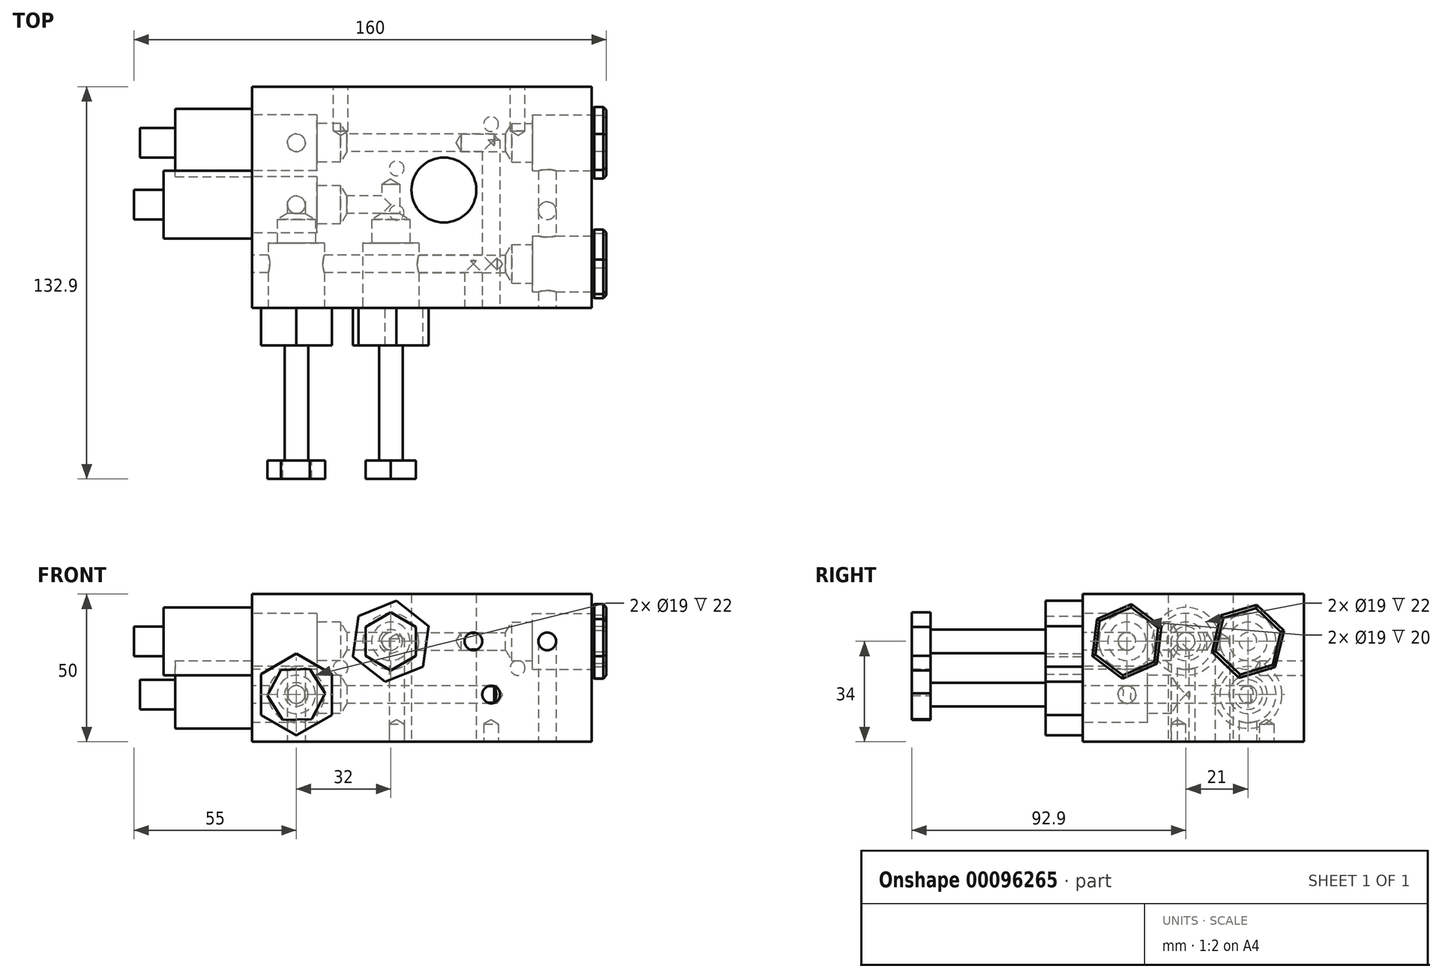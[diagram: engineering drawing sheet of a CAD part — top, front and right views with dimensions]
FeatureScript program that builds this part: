
annotation { "Feature Type Name" : "Feature", "Feature Type Description" : "" }
export const myFeature = defineFeature(function(context is Context, id is Id, definition is map)
    precondition{}
    {
        {
            var Q0;
            Q0=qCreatedBy(makeId("Top.planeOp"),FACE);
            var sketch = newSketch(context, id + "F0", { "sketchPlane" : qUnion([Q0])});
            skLineSegment(sketch, "E0.rect.bottom", {"start": v(50, 35) * mm, "end": v(-65, 35) * mm});
            skLineSegment(sketch, "E0.rect.top", {"start": v(50, -40) * mm, "end": v(-65, -40) * mm});
            skLineSegment(sketch, "E0.rect.left", {"start": v(50, 35) * mm, "end": v(50, -40) * mm});
            skLineSegment(sketch, "E0.rect.right", {"start": v(-65, 35) * mm, "end": v(-65, -40) * mm});
            skPoint(sketch, "E0.rect.middle", {"position": v(0, 0) * mm});
            skSolve(sketch);
        }
        {
            var Q0;
            Q0=makeQuery(id+"F0.imprint","IMPRINT",FACE,{"disambiguationData":[TD([[makeQuery(id+"F0.imprint","IMPRINT",EDGE,{"derivedFrom":sQuery(id+"F0.wireOp",EDGE,"E0.rect.bottom")}),1.0]])]});
            var Q1;
            Q1=makeQuery(id+"F0.imprint","IMPRINT",FACE,{"disambiguationData":[TD([[makeQuery(id+"F0.imprint","IMPRINT",EDGE,{"derivedFrom":sQuery(id+"F0.wireOp",EDGE,"7588558b-6d4b-4371-8287-17bf13519ebf.1.0.0")}),1.0]])]});
            var Q2;
            Q2=makeQuery(id+"F0.imprint","IMPRINT",FACE,{"disambiguationData":[TD([[makeQuery(id+"F0.imprint","IMPRINT",EDGE,{"derivedFrom":sQuery(id+"F0.wireOp",EDGE,"7588558b-6d4b-4371-8287-17bf13519ebf.1.1.0")}),1.0]])]});
            var Q3;
            Q3=makeQuery(id+"F0.imprint","IMPRINT",FACE,{"disambiguationData":[TD([[makeQuery(id+"F0.imprint","IMPRINT",EDGE,{"derivedFrom":sQuery(id+"F0.wireOp",EDGE,"f2f94a69-6f03-48d5-8e05-4ef8c2e551b9")}),1.0]])]});
            var Q4;
            Q4=makeQuery(id+"F0.imprint","IMPRINT",FACE,{"disambiguationData":[TD([[makeQuery(id+"F0.imprint","IMPRINT",EDGE,{"derivedFrom":sQuery(id+"F0.wireOp",EDGE,"7588558b-6d4b-4371-8287-17bf13519ebf.0.1.0")}),1.0]])]});
            extrude(context, id + "F1", {"entities" : qUnion([Q0, Q1, Q2, Q3, Q4]), "depth" : 50 * mm});
        }
        {
            var Q0;
            Q0=makeQuery(id+"F1.opExtrude","CAP_FACE",FACE,{"disambiguationData":[OSD([sQuery(id+"F0.wireOp",EDGE,"E0.rect.bottom"),sQuery(id+"F0.wireOp",EDGE,"E0.rect.top"),sQuery(id+"F0.wireOp",EDGE,"E0.rect.left"),sQuery(id+"F0.wireOp",EDGE,"E0.rect.right"),sQuery(id+"F0.wireOp",EDGE,"fc206ab4-4ad2-4e77-9b30-4fb9f0a5357b")])],"isStart":true});
            var sketch = newSketch(context, id + "F2", { "sketchPlane" : qUnion([Q0])});
            skCircle(sketch, "E1", {"center": v(-16, 7.68) * mm, "radius": 2.75 * mm});
            skCircle(sketch, "E2", {"center": v(16, -22.32) * mm, "radius": 2.75 * mm});
            skCircle(sketch, "E3", {"center": v(-16, -7.32) * mm, "radius": 3 * mm});
            skPoint(sketch, "E4", {"position": v(-50, 5) * mm});
            skPoint(sketch, "E5", {"position": v(35, 7) * mm});
            skPoint(sketch, "E6", {"position": v(-50, -16) * mm});
            skLineSegment(sketch, "E7", {"start": v(-16, -7.32) * mm, "end": v(44.16, -7.32) * mm, "construction": true});
            skLineSegment(sketch, "E8", {"start": v(-16, -16.9) * mm, "end": v(-16, 32.16) * mm, "construction": true});
            skPoint(sketch, "E9.0", {"position": v(0, 0) * mm});
            skLineSegment(sketch, "E10", {"start": v(-80.64, 0) * mm, "end": v(41.16, 0) * mm, "construction": true});
            skSolve(sketch);
        }
        {
            var Q0;
            Q0=sQuery(id+"F2.wireOp",VERTEX,"E3.center");
            var Q1;
            Q1=makeQuery(id+"F1.opExtrude","SWEPT_BODY",BODY,{"disambiguationData":[OSD([sQuery(id+"F0.wireOp",EDGE,"E0.rect.bottom"),sQuery(id+"F0.wireOp",EDGE,"E0.rect.top"),sQuery(id+"F0.wireOp",EDGE,"E0.rect.left"),sQuery(id+"F0.wireOp",EDGE,"E0.rect.right"),sQuery(id+"F0.wireOp",EDGE,"fc206ab4-4ad2-4e77-9b30-4fb9f0a5357b")])]});
            hole(context, id + "F3", {"style" : HoleStyle.SIMPLE, "holeDiameter" : 5 * mm, "endStyle" : HoleEndStyle.BLIND, "holeDepth" : 35 * mm, "locations" : qUnion([Q0]), "scope" : qUnion([Q1])});
        }
        {
            var Q0;
            Q0=makeQuery(id+"F1.opExtrude","SWEPT_FACE",FACE,{"disambiguationData":[OSD([sQuery(id+"F0.wireOp",EDGE,"E0.rect.bottom")])]});
            var sketch = newSketch(context, id + "F4", { "sketchPlane" : qUnion([Q0])});
            skLineSegment(sketch, "E11", {"start": v(65, 16) * mm, "end": v(-50, 16) * mm, "construction": true});
            skPoint(sketch, "E12", {"position": v(-30, 16) * mm});
            skPoint(sketch, "E13", {"position": v(50, 16) * mm});
            skSolve(sketch);
        }
        {
            var Q0;
            Q0=makeQuery(id+"F1.opExtrude","SWEPT_FACE",FACE,{"disambiguationData":[OSD([sQuery(id+"F0.wireOp",EDGE,"E0.rect.left")])]});
            var sketch = newSketch(context, id + "F5", { "sketchPlane" : qUnion([Q0])});
            skLineSegment(sketch, "E14", {"start": v(-25, 34) * mm, "end": v(16, 34) * mm, "construction": true});
            skPoint(sketch, "E15", {"position": v(16, 34) * mm});
            skPoint(sketch, "E16", {"position": v(-25, 34) * mm});
            skPoint(sketch, "E17.orphan", {"position": v(35, 34) * mm});
            skCircle(sketch, "E18.cCircle", {"center": v(-25, 34) * mm, "radius": 11 * mm, "construction": true});
            skLineSegment(sketch, "E18.0", {"start": v(-35.19, 41.58) * mm, "end": v(-23.53, 46.62) * mm});
            skLineSegment(sketch, "E18.1", {"start": v(-23.53, 46.62) * mm, "end": v(-13.34, 39.03) * mm});
            skLineSegment(sketch, "E18.2", {"start": v(-13.34, 39.03) * mm, "end": v(-14.81, 26.42) * mm});
            skLineSegment(sketch, "E18.3", {"start": v(-14.81, 26.42) * mm, "end": v(-26.47, 21.38) * mm});
            skLineSegment(sketch, "E18.4", {"start": v(-26.47, 21.38) * mm, "end": v(-36.66, 28.97) * mm});
            skLineSegment(sketch, "E18.5", {"start": v(-36.66, 28.97) * mm, "end": v(-35.19, 41.58) * mm});
            skPoint(sketch, "E18.0.midPoint", {"position": v(-29.36, 44.1) * mm});
            skCircle(sketch, "E19.cCircle", {"center": v(16, 34) * mm, "radius": 11 * mm, "construction": true});
            skLineSegment(sketch, "E19.0", {"start": v(6.8, 42.75) * mm, "end": v(18.98, 46.35) * mm});
            skLineSegment(sketch, "E19.1", {"start": v(18.98, 46.35) * mm, "end": v(28.18, 37.6) * mm});
            skLineSegment(sketch, "E19.2", {"start": v(28.18, 37.6) * mm, "end": v(25.2, 25.25) * mm});
            skLineSegment(sketch, "E19.3", {"start": v(25.2, 25.25) * mm, "end": v(13.02, 21.65) * mm});
            skLineSegment(sketch, "E19.4", {"start": v(13.02, 21.65) * mm, "end": v(3.82, 30.4) * mm});
            skLineSegment(sketch, "E19.5", {"start": v(3.82, 30.4) * mm, "end": v(6.8, 42.75) * mm});
            skPoint(sketch, "E19.0.midPoint", {"position": v(12.89, 44.55) * mm});
            skSolve(sketch);
        }
        {
            var Q0;
            Q0=sQuery(id+"F5.wireOp",VERTEX,"E15");
            var Q1;
            Q1=sQuery(id+"F5.wireOp",VERTEX,"E16");
            var Q2;
            Q2=makeQuery(id+"F1.opExtrude","SWEPT_BODY",BODY,{"disambiguationData":[OSD([sQuery(id+"F0.wireOp",EDGE,"E0.rect.bottom"),sQuery(id+"F0.wireOp",EDGE,"E0.rect.top"),sQuery(id+"F0.wireOp",EDGE,"E0.rect.left"),sQuery(id+"F0.wireOp",EDGE,"E0.rect.right"),sQuery(id+"F0.wireOp",EDGE,"fc206ab4-4ad2-4e77-9b30-4fb9f0a5357b")])]});
            hole(context, id + "F6", {"style" : HoleStyle.C_BORE, "endStyle" : HoleEndStyle.BLIND, "holeDiameter" : 13 * mm, "cBoreDiameter" : 19 * mm, "cBoreDepth" : 20 * mm, "holeDepth" : 27 * mm, "locations" : qUnion([Q0, Q1]), "scope" : qUnion([Q2])});
        }
        {
            var Q0;
            Q0=makeQuery(id+"F1.opExtrude","SWEPT_FACE",FACE,{"disambiguationData":[OSD([sQuery(id+"F0.wireOp",EDGE,"E0.rect.top")])]});
            var sketch = newSketch(context, id + "F7", { "sketchPlane" : qUnion([Q0])});
            skLineSegment(sketch, "E20", {"start": v(-65, 34) * mm, "end": v(50, 34) * mm, "construction": true});
            skLineSegment(sketch, "E21", {"start": v(-65, 16) * mm, "end": v(50, 16) * mm, "construction": true});
            skPoint(sketch, "E22", {"position": v(-50, 16) * mm});
            skPoint(sketch, "E23", {"position": v(-18, 34) * mm});
            skPoint(sketch, "E24", {"position": v(35, 34) * mm});
            skPoint(sketch, "E25", {"position": v(10, 34) * mm});
            skPoint(sketch, "E26", {"position": v(16, 16) * mm});
            skSolve(sketch);
        }
        {
            var Q0;
            Q0=sQuery(id+"F7.wireOp",VERTEX,"E26");
            var Q1;
            Q1=makeQuery(id+"F1.opExtrude","SWEPT_BODY",BODY,{"disambiguationData":[OSD([sQuery(id+"F0.wireOp",EDGE,"E0.rect.bottom"),sQuery(id+"F0.wireOp",EDGE,"E0.rect.top"),sQuery(id+"F0.wireOp",EDGE,"E0.rect.left"),sQuery(id+"F0.wireOp",EDGE,"E0.rect.right"),sQuery(id+"F0.wireOp",EDGE,"fc206ab4-4ad2-4e77-9b30-4fb9f0a5357b")])]});
            hole(context, id + "F8", {"style" : HoleStyle.SIMPLE, "holeDiameter" : 6 * mm, "endStyle" : HoleEndStyle.BLIND, "holeDepth" : 57 * mm, "locations" : qUnion([Q0]), "scope" : qUnion([Q1])});
        }
        {
            var Q0;
            Q0=makeQuery(id+"F1.opExtrude","SWEPT_FACE",FACE,{"disambiguationData":[OSD([sQuery(id+"F0.wireOp",EDGE,"E0.rect.right")])]});
            var sketch = newSketch(context, id + "F9", { "sketchPlane" : qUnion([Q0])});
            skPoint(sketch, "E27", {"position": v(25, 16) * mm});
            skPoint(sketch, "E28", {"position": v(5, 34) * mm});
            skPoint(sketch, "E29", {"position": v(-16, 16) * mm});
            skCircle(sketch, "E30", {"center": v(5, 34) * mm, "radius": 11.5 * mm});
            skSolve(sketch);
        }
        {
            var Q0;
            Q0=sQuery(id+"F9.wireOp",VERTEX,"E27");
            var Q1;
            Q1=makeQuery(id+"F1.opExtrude","SWEPT_BODY",BODY,{"disambiguationData":[OSD([sQuery(id+"F0.wireOp",EDGE,"E0.rect.bottom"),sQuery(id+"F0.wireOp",EDGE,"E0.rect.top"),sQuery(id+"F0.wireOp",EDGE,"E0.rect.left"),sQuery(id+"F0.wireOp",EDGE,"E0.rect.right"),sQuery(id+"F0.wireOp",EDGE,"fc206ab4-4ad2-4e77-9b30-4fb9f0a5357b")])]});
            hole(context, id + "F10", {"style" : HoleStyle.SIMPLE, "endStyle" : HoleEndStyle.BLIND, "holeDiameter" : 6 * mm, "holeDepth" : 83 * mm, "locations" : qUnion([Q0]), "scope" : qUnion([Q1])});
        }
        {
            var Q0;
            Q0=sQuery(id+"F7.wireOp",VERTEX,"E22");
            var Q1;
            Q1=sQuery(id+"F7.wireOp",VERTEX,"E23");
            var Q2;
            Q2=makeQuery(id+"F1.opExtrude","SWEPT_BODY",BODY,{"disambiguationData":[OSD([sQuery(id+"F0.wireOp",EDGE,"E0.rect.bottom"),sQuery(id+"F0.wireOp",EDGE,"E0.rect.top"),sQuery(id+"F0.wireOp",EDGE,"E0.rect.left"),sQuery(id+"F0.wireOp",EDGE,"E0.rect.right"),sQuery(id+"F0.wireOp",EDGE,"fc206ab4-4ad2-4e77-9b30-4fb9f0a5357b")])]});
            hole(context, id + "F11", {"style" : HoleStyle.C_BORE, "endStyle" : HoleEndStyle.BLIND, "holeDiameter" : 13 * mm, "cBoreDiameter" : 19 * mm, "cBoreDepth" : 22 * mm, "holeDepth" : 30 * mm, "locations" : qUnion([Q0, Q1]), "scope" : qUnion([Q2])});
        }
        {
            var Q0;
            Q0=sQuery(id+"F7.wireOp",VERTEX,"E22");
            var Q1;
            Q1=makeQuery(id+"F1.opExtrude","SWEPT_BODY",BODY,{"disambiguationData":[OSD([sQuery(id+"F0.wireOp",EDGE,"E0.rect.bottom"),sQuery(id+"F0.wireOp",EDGE,"E0.rect.top"),sQuery(id+"F0.wireOp",EDGE,"E0.rect.left"),sQuery(id+"F0.wireOp",EDGE,"E0.rect.right"),sQuery(id+"F0.wireOp",EDGE,"fc206ab4-4ad2-4e77-9b30-4fb9f0a5357b")])]});
            hole(context, id + "F12", {"style" : HoleStyle.SIMPLE, "endStyle" : HoleEndStyle.BLIND, "holeDiameter" : 6 * mm, "holeDepth" : 4 * mm, "locations" : qUnion([Q0]), "scope" : qUnion([Q1])});
        }
        {
            var Q0;
            Q0=sQuery(id+"F5.wireOp",VERTEX,"E15");
            var Q1;
            Q1=makeQuery(id+"F1.opExtrude","SWEPT_BODY",BODY,{"disambiguationData":[OSD([sQuery(id+"F0.wireOp",EDGE,"E0.rect.bottom"),sQuery(id+"F0.wireOp",EDGE,"E0.rect.top"),sQuery(id+"F0.wireOp",EDGE,"E0.rect.left"),sQuery(id+"F0.wireOp",EDGE,"E0.rect.right"),sQuery(id+"F0.wireOp",EDGE,"fc206ab4-4ad2-4e77-9b30-4fb9f0a5357b")])]});
            hole(context, id + "F13", {"style" : HoleStyle.SIMPLE, "endStyle" : HoleEndStyle.BLIND, "holeDiameter" : 6 * mm, "holeDepth" : 15 * mm, "locations" : qUnion([Q0]), "scope" : qUnion([Q1])});
        }
        {
            var Q0;
            Q0=sQuery(id+"F7.wireOp",VERTEX,"E25");
            var Q1;
            Q1=makeQuery(id+"F1.opExtrude","SWEPT_BODY",BODY,{"disambiguationData":[OSD([sQuery(id+"F0.wireOp",EDGE,"E0.rect.bottom"),sQuery(id+"F0.wireOp",EDGE,"E0.rect.top"),sQuery(id+"F0.wireOp",EDGE,"E0.rect.left"),sQuery(id+"F0.wireOp",EDGE,"E0.rect.right"),sQuery(id+"F0.wireOp",EDGE,"fc206ab4-4ad2-4e77-9b30-4fb9f0a5357b")])]});
            hole(context, id + "F14", {"style" : HoleStyle.SIMPLE, "endStyle" : HoleEndStyle.BLIND, "holeDiameter" : 6 * mm, "holeDepth" : 16 * mm, "locations" : qUnion([Q0]), "scope" : qUnion([Q1])});
        }
        {
            var Q0;
            Q0=sQuery(id+"F5.wireOp",VERTEX,"E16");
            var Q1;
            Q1=makeQuery(id+"F1.opExtrude","SWEPT_BODY",BODY,{"disambiguationData":[OSD([sQuery(id+"F0.wireOp",EDGE,"E0.rect.bottom"),sQuery(id+"F0.wireOp",EDGE,"E0.rect.top"),sQuery(id+"F0.wireOp",EDGE,"E0.rect.left"),sQuery(id+"F0.wireOp",EDGE,"E0.rect.right"),sQuery(id+"F0.wireOp",EDGE,"fc206ab4-4ad2-4e77-9b30-4fb9f0a5357b")])]});
            hole(context, id + "F15", {"style" : HoleStyle.SIMPLE, "endStyle" : HoleEndStyle.BLIND, "holeDiameter" : 6 * mm, "holeDepth" : 30 * mm, "locations" : qUnion([Q0]), "scope" : qUnion([Q1])});
        }
        {
            var Q0;
            Q0=sQuery(id+"F7.wireOp",VERTEX,"E24");
            var Q1;
            Q1=makeQuery(id+"F1.opExtrude","SWEPT_BODY",BODY,{"disambiguationData":[OSD([sQuery(id+"F0.wireOp",EDGE,"E0.rect.bottom"),sQuery(id+"F0.wireOp",EDGE,"E0.rect.top"),sQuery(id+"F0.wireOp",EDGE,"E0.rect.left"),sQuery(id+"F0.wireOp",EDGE,"E0.rect.right"),sQuery(id+"F0.wireOp",EDGE,"fc206ab4-4ad2-4e77-9b30-4fb9f0a5357b")])]});
            hole(context, id + "F16", {"style" : HoleStyle.SIMPLE, "endStyle" : HoleEndStyle.BLIND, "holeDiameter" : 6 * mm, "holeDepth" : 50 * mm, "locations" : qUnion([Q0]), "scope" : qUnion([Q1])});
        }
        {
            var Q0;
            Q0=sQuery(id+"F5.wireOp",VERTEX,"53e86b82-a842-4255-912a-a7488f70ac65");
            var Q1;
            Q1=sQuery(id+"F2.wireOp",VERTEX,"E5");
            var Q2;
            Q2=makeQuery(id+"F1.opExtrude","SWEPT_BODY",BODY,{"disambiguationData":[OSD([sQuery(id+"F0.wireOp",EDGE,"E0.rect.bottom"),sQuery(id+"F0.wireOp",EDGE,"E0.rect.top"),sQuery(id+"F0.wireOp",EDGE,"E0.rect.left"),sQuery(id+"F0.wireOp",EDGE,"E0.rect.right"),sQuery(id+"F0.wireOp",EDGE,"fc206ab4-4ad2-4e77-9b30-4fb9f0a5357b")])]});
            hole(context, id + "F17", {"style" : HoleStyle.SIMPLE, "endStyle" : HoleEndStyle.BLIND, "holeDiameter" : 6 * mm, "holeDepth" : 34 * mm, "locations" : qUnion([Q0, Q1]), "scope" : qUnion([Q2])});
        }
        {
            var Q0;
            Q0=sQuery(id+"F9.wireOp",VERTEX,"E28");
            var Q1;
            Q1=makeQuery(id+"F1.opExtrude","SWEPT_BODY",BODY,{"disambiguationData":[OSD([sQuery(id+"F0.wireOp",EDGE,"E0.rect.bottom"),sQuery(id+"F0.wireOp",EDGE,"E0.rect.top"),sQuery(id+"F0.wireOp",EDGE,"E0.rect.left"),sQuery(id+"F0.wireOp",EDGE,"E0.rect.right"),sQuery(id+"F0.wireOp",EDGE,"fc206ab4-4ad2-4e77-9b30-4fb9f0a5357b")])]});
            hole(context, id + "F18", {"style" : HoleStyle.C_BORE, "endStyle" : HoleEndStyle.BLIND, "holeDiameter" : 13 * mm, "cBoreDiameter" : 19 * mm, "cBoreDepth" : 22 * mm, "holeDepth" : 30 * mm, "locations" : qUnion([Q0]), "scope" : qUnion([Q1])});
        }
        {
            var Q0;
            Q0=sQuery(id+"F9.wireOp",VERTEX,"E29");
            var Q1;
            Q1=makeQuery(id+"F1.opExtrude","SWEPT_BODY",BODY,{"disambiguationData":[OSD([sQuery(id+"F0.wireOp",EDGE,"E0.rect.bottom"),sQuery(id+"F0.wireOp",EDGE,"E0.rect.top"),sQuery(id+"F0.wireOp",EDGE,"E0.rect.left"),sQuery(id+"F0.wireOp",EDGE,"E0.rect.right")])]});
            hole(context, id + "F19", {"style" : HoleStyle.C_BORE, "endStyle" : HoleEndStyle.BLIND, "holeDiameter" : 13 * mm, "cBoreDiameter" : 19 * mm, "cBoreDepth" : 22 * mm, "holeDepth" : 30 * mm, "startFromSketch" : true, "locations" : qUnion([Q0]), "scope" : qUnion([Q1])});
        }
        {
            var Q0;
            Q0=sQuery(id+"F9.wireOp",VERTEX,"E28");
            var Q1;
            Q1=makeQuery(id+"F1.opExtrude","SWEPT_BODY",BODY,{"disambiguationData":[OSD([sQuery(id+"F0.wireOp",EDGE,"E0.rect.bottom"),sQuery(id+"F0.wireOp",EDGE,"E0.rect.top"),sQuery(id+"F0.wireOp",EDGE,"E0.rect.left"),sQuery(id+"F0.wireOp",EDGE,"E0.rect.right"),sQuery(id+"F0.wireOp",EDGE,"fc206ab4-4ad2-4e77-9b30-4fb9f0a5357b")])]});
            hole(context, id + "F20", {"style" : HoleStyle.SIMPLE, "endStyle" : HoleEndStyle.BLIND, "holeDiameter" : 6 * mm, "holeDepth" : 15 * mm, "locations" : qUnion([Q0]), "scope" : qUnion([Q1])});
        }
        {
            var Q0;
            Q0=sQuery(id+"F2.wireOp",VERTEX,"E4");
            var Q1;
            Q1=makeQuery(id+"F1.opExtrude","SWEPT_BODY",BODY,{"disambiguationData":[OSD([sQuery(id+"F0.wireOp",EDGE,"E0.rect.bottom"),sQuery(id+"F0.wireOp",EDGE,"E0.rect.top"),sQuery(id+"F0.wireOp",EDGE,"E0.rect.left"),sQuery(id+"F0.wireOp",EDGE,"E0.rect.right"),sQuery(id+"F0.wireOp",EDGE,"fc206ab4-4ad2-4e77-9b30-4fb9f0a5357b")])]});
            hole(context, id + "F21", {"style" : HoleStyle.SIMPLE, "endStyle" : HoleEndStyle.BLIND, "holeDiameter" : 6 * mm, "holeDepth" : 35 * mm, "locations" : qUnion([Q0]), "scope" : qUnion([Q1])});
        }
        {
            var Q0;
            Q0=sQuery(id+"F7.wireOp",VERTEX,"E23");
            var Q1;
            Q1=makeQuery(id+"F1.opExtrude","SWEPT_BODY",BODY,{"disambiguationData":[OSD([sQuery(id+"F0.wireOp",EDGE,"E0.rect.bottom"),sQuery(id+"F0.wireOp",EDGE,"E0.rect.top"),sQuery(id+"F0.wireOp",EDGE,"E0.rect.left"),sQuery(id+"F0.wireOp",EDGE,"E0.rect.right"),sQuery(id+"F0.wireOp",EDGE,"fc206ab4-4ad2-4e77-9b30-4fb9f0a5357b")])]});
            hole(context, id + "F22", {"style" : HoleStyle.SIMPLE, "endStyle" : HoleEndStyle.BLIND, "holeDiameter" : 6 * mm, "holeDepth" : 4 * mm, "locations" : qUnion([Q0]), "scope" : qUnion([Q1])});
        }
        {
            var Q0;
            Q0=makeQuery(id+"F1.opExtrude","SWEPT_FACE",FACE,{"disambiguationData":[OSD([sQuery(id+"F0.wireOp",EDGE,"E0.rect.bottom")])]});
            var sketch = newSketch(context, id + "F23", { "sketchPlane" : qUnion([Q0])});
            skPoint(sketch, "E31", {"position": v(-25, 25) * mm});
            skPoint(sketch, "E32.1.0.0", {"position": v(35, 25) * mm});
            skLineSegment(sketch, "E32.direction1", {"start": v(-25, 25) * mm, "end": v(35, 25) * mm, "construction": true});
            skSolve(sketch);
        }
        {
            var Q0;
            Q0=sQuery(id+"F23.wireOp",VERTEX,"E32.1.0.0");
            var Q1;
            Q1=sQuery(id+"F23.wireOp",VERTEX,"E31");
            var Q2;
            Q2=makeQuery(id+"F1.opExtrude","SWEPT_BODY",BODY,{"disambiguationData":[OSD([sQuery(id+"F0.wireOp",EDGE,"E0.rect.bottom"),sQuery(id+"F0.wireOp",EDGE,"E0.rect.top"),sQuery(id+"F0.wireOp",EDGE,"E0.rect.left"),sQuery(id+"F0.wireOp",EDGE,"E0.rect.right"),sQuery(id+"F0.wireOp",EDGE,"fc206ab4-4ad2-4e77-9b30-4fb9f0a5357b")])]});
            hole(context, id + "F24", {"style" : HoleStyle.SIMPLE, "endStyle" : HoleEndStyle.BLIND, "holeDiameter" : 5 * mm, "holeDepth" : 15 * mm, "locations" : qUnion([Q0, Q1]), "scope" : qUnion([Q2])});
        }
        {
            var Q0;
            Q0=sQuery(id+"F0.wireOp",VERTEX,"E0.rect.middle");
            var Q1;
            Q1=makeQuery(id+"F1.opExtrude","SWEPT_BODY",BODY,{"disambiguationData":[OSD([sQuery(id+"F0.wireOp",EDGE,"E0.rect.bottom"),sQuery(id+"F0.wireOp",EDGE,"E0.rect.top"),sQuery(id+"F0.wireOp",EDGE,"E0.rect.left"),sQuery(id+"F0.wireOp",EDGE,"E0.rect.right")])]});
            hole(context, id + "F25", {"style" : HoleStyle.SIMPLE, "endStyle" : HoleEndStyle.THROUGH, "oppositeDirection" : true, "holeDiameter" : 22 * mm, "locations" : qUnion([Q0]), "scope" : qUnion([Q1]), "isTappedThrough" : true});
        }
        {
            var Q0;
            {var subQ0=sQuery(id+"F0.wireOp",EDGE,"E0.rect.right");Q0=makeQuery(id+"F9.imprint","IMPRINT",FACE,{"disambiguationData":[TD([[makeQuery(id+"F9.imprint","IMPRINT",EDGE,{"derivedFrom":makeQuery(id+"F1.opExtrude","CAP_EDGE",EDGE,{"disambiguationData":[OSD([subQ0])],"isStart":true})}),1.0]])]});}
            var sketch = newSketch(context, id + "F26", { "sketchPlane" : qUnion([Q0])});
            skCircle(sketch, "E33", {"center": v(-16, 16) * mm, "radius": 11.5 * mm});
            skSolve(sketch);
        }
        {
            var Q0;
            Q0=makeQuery(id+"F26.imprint","IMPRINT",FACE,{"disambiguationData":[TD([[makeQuery(id+"F26.imprint","IMPRINT",EDGE,{"derivedFrom":sQuery(id+"F26.wireOp",EDGE,"E33")}),1.0]])]});
            extrude(context, id + "F27", {"entities" : qUnion([Q0]), "depth" : 26 * mm});
        }
        {
            var Q0;
            Q0=makeQuery(id+"F27.opExtrude","CAP_FACE",FACE,{"disambiguationData":[OSD([sQuery(id+"F26.wireOp",EDGE,"E33")])],"isStart":false});
            var sketch = newSketch(context, id + "F28", { "sketchPlane" : qUnion([Q0])});
            skCircle(sketch, "E34", {"center": v(-16, 16) * mm, "radius": 5 * mm});
            skSolve(sketch);
        }
        {
            var Q0;
            Q0=sQuery(id+"F9.wireOp",VERTEX,"E29");
            var Q1;
            Q1=makeQuery(id+"F1.opExtrude","SWEPT_BODY",BODY,{"disambiguationData":[OSD([sQuery(id+"F0.wireOp",EDGE,"E0.rect.bottom"),sQuery(id+"F0.wireOp",EDGE,"E0.rect.top"),sQuery(id+"F0.wireOp",EDGE,"E0.rect.left"),sQuery(id+"F0.wireOp",EDGE,"E0.rect.right")])]});
            hole(context, id + "F29", {"style" : HoleStyle.SIMPLE, "endStyle" : HoleEndStyle.BLIND, "holeDiameter" : 6 * mm, "holeDepth" : 82 * mm, "startFromSketch" : true, "locations" : qUnion([Q0]), "scope" : qUnion([Q1])});
        }
        {
            var Q0;
            Q0=makeQuery(id+"F5.imprint","IMPRINT",FACE,{"disambiguationData":[TD([[makeQuery(id+"F5.imprint","IMPRINT",EDGE,{"derivedFrom":sQuery(id+"F5.wireOp",EDGE,"E18.0")}),-1.0]])]});
            var Q1;
            Q1=makeQuery(id+"F5.imprint","IMPRINT",FACE,{"disambiguationData":[TD([[makeQuery(id+"F5.imprint","IMPRINT",EDGE,{"derivedFrom":sQuery(id+"F5.wireOp",EDGE,"E19.0")}),-1.0]])]});
            extrude(context, id + "F30", {"entities" : qUnion([Q0, Q1]), "depth" : 5 * mm});
        }
        {
            var Q0;
            Q0=makeQuery(id+"F30.opExtrude","CAP_EDGE",EDGE,{"disambiguationData":[OSD([sQuery(id+"F5.wireOp",EDGE,"E18.3")])],"isStart":true});
            var Q1;
            Q1=makeQuery(id+"F30.opExtrude","CAP_EDGE",EDGE,{"disambiguationData":[OSD([sQuery(id+"F5.wireOp",EDGE,"E18.4")])],"isStart":true});
            var Q2;
            Q2=makeQuery(id+"F30.opExtrude","CAP_EDGE",EDGE,{"disambiguationData":[OSD([sQuery(id+"F5.wireOp",EDGE,"E18.5")])],"isStart":true});
            var Q3;
            Q3=makeQuery(id+"F30.opExtrude","CAP_EDGE",EDGE,{"disambiguationData":[OSD([sQuery(id+"F5.wireOp",EDGE,"E18.4")])],"isStart":false});
            var Q4;
            Q4=makeQuery(id+"F30.opExtrude","CAP_EDGE",EDGE,{"disambiguationData":[OSD([sQuery(id+"F5.wireOp",EDGE,"E18.3")])],"isStart":false});
            var Q5;
            Q5=makeQuery(id+"F30.opExtrude","CAP_EDGE",EDGE,{"disambiguationData":[OSD([sQuery(id+"F5.wireOp",EDGE,"E18.2")])],"isStart":false});
            var Q6;
            Q6=makeQuery(id+"F30.opExtrude","CAP_EDGE",EDGE,{"disambiguationData":[OSD([sQuery(id+"F5.wireOp",EDGE,"E18.1")])],"isStart":false});
            var Q7;
            Q7=makeQuery(id+"F30.opExtrude","CAP_EDGE",EDGE,{"disambiguationData":[OSD([sQuery(id+"F5.wireOp",EDGE,"E18.0")])],"isStart":false});
            var Q8;
            Q8=makeQuery(id+"F30.opExtrude","CAP_EDGE",EDGE,{"disambiguationData":[OSD([sQuery(id+"F5.wireOp",EDGE,"E18.5")])],"isStart":false});
            var Q9;
            Q9=makeQuery(id+"F30.opExtrude","CAP_EDGE",EDGE,{"disambiguationData":[OSD([sQuery(id+"F5.wireOp",EDGE,"E18.0")])],"isStart":true});
            var Q10;
            Q10=makeQuery(id+"F30.opExtrude","CAP_EDGE",EDGE,{"disambiguationData":[OSD([sQuery(id+"F5.wireOp",EDGE,"E18.1")])],"isStart":true});
            var Q11;
            Q11=makeQuery(id+"F30.opExtrude","CAP_EDGE",EDGE,{"disambiguationData":[OSD([sQuery(id+"F5.wireOp",EDGE,"E18.2")])],"isStart":true});
            var Q12;
            Q12=makeQuery(id+"F30.opExtrude","CAP_EDGE",EDGE,{"disambiguationData":[OSD([sQuery(id+"F5.wireOp",EDGE,"E19.4")])],"isStart":false});
            var Q13;
            Q13=makeQuery(id+"F30.opExtrude","CAP_EDGE",EDGE,{"disambiguationData":[OSD([sQuery(id+"F5.wireOp",EDGE,"E19.4")])],"isStart":true});
            var Q14;
            Q14=makeQuery(id+"F30.opExtrude","CAP_EDGE",EDGE,{"disambiguationData":[OSD([sQuery(id+"F5.wireOp",EDGE,"E19.3")])],"isStart":false});
            var Q15;
            Q15=makeQuery(id+"F30.opExtrude","CAP_EDGE",EDGE,{"disambiguationData":[OSD([sQuery(id+"F5.wireOp",EDGE,"E19.3")])],"isStart":true});
            var Q16;
            Q16=makeQuery(id+"F30.opExtrude","CAP_EDGE",EDGE,{"disambiguationData":[OSD([sQuery(id+"F5.wireOp",EDGE,"E19.2")])],"isStart":false});
            var Q17;
            Q17=makeQuery(id+"F30.opExtrude","CAP_EDGE",EDGE,{"disambiguationData":[OSD([sQuery(id+"F5.wireOp",EDGE,"E19.2")])],"isStart":true});
            var Q18;
            Q18=makeQuery(id+"F30.opExtrude","CAP_EDGE",EDGE,{"disambiguationData":[OSD([sQuery(id+"F5.wireOp",EDGE,"E19.1")])],"isStart":false});
            var Q19;
            Q19=makeQuery(id+"F30.opExtrude","CAP_EDGE",EDGE,{"disambiguationData":[OSD([sQuery(id+"F5.wireOp",EDGE,"E19.1")])],"isStart":true});
            var Q20;
            Q20=makeQuery(id+"F30.opExtrude","CAP_EDGE",EDGE,{"disambiguationData":[OSD([sQuery(id+"F5.wireOp",EDGE,"E19.5")])],"isStart":false});
            var Q21;
            Q21=makeQuery(id+"F30.opExtrude","CAP_EDGE",EDGE,{"disambiguationData":[OSD([sQuery(id+"F5.wireOp",EDGE,"E19.5")])],"isStart":true});
            var Q22;
            Q22=makeQuery(id+"F30.opExtrude","CAP_EDGE",EDGE,{"disambiguationData":[OSD([sQuery(id+"F5.wireOp",EDGE,"E19.0")])],"isStart":true});
            var Q23;
            Q23=makeQuery(id+"F30.opExtrude","CAP_EDGE",EDGE,{"disambiguationData":[OSD([sQuery(id+"F5.wireOp",EDGE,"E19.0")])],"isStart":false});
            chamfer(context, id + "F31", {"entities" : qUnion([Q0, Q1, Q2, Q3, Q4, Q5, Q6, Q7, Q8, Q9, Q10, Q11, Q12, Q13, Q14, Q15, Q16, Q17, Q18, Q19, Q20, Q21, Q22, Q23]), "width" : 1 * mm, "tangentPropagation" : true});
        }
        {
            var Q0;
            Q0=makeQuery(id+"F28.imprint","IMPRINT",FACE,{"disambiguationData":[TD([[makeQuery(id+"F28.imprint","IMPRINT",EDGE,{"derivedFrom":sQuery(id+"F28.wireOp",EDGE,"E34")}),1.0]])]});
            extrude(context, id + "F32", {"entities" : qUnion([Q0]), "operationType" : NewBodyOperationType.ADD, "depth" : 12 * mm});
        }
        {
            var Q0;
            Q0=makeQuery(id+"F9.imprint","IMPRINT",FACE,{"disambiguationData":[TD([[makeQuery(id+"F9.imprint","IMPRINT",EDGE,{"derivedFrom":sQuery(id+"F9.wireOp",EDGE,"E30")}),1.0]])]});
            extrude(context, id + "F33", {"entities" : qUnion([Q0]), "depth" : 30 * mm});
        }
        {
            var Q0;
            Q0=makeQuery(id+"F33.opExtrude","CAP_FACE",FACE,{"disambiguationData":[OSD([sQuery(id+"F9.wireOp",EDGE,"E30")])],"isStart":false});
            var sketch = newSketch(context, id + "F34", { "sketchPlane" : qUnion([Q0])});
            skCircle(sketch, "E35", {"center": v(5, 34) * mm, "radius": 5 * mm});
            skSolve(sketch);
        }
        {
            var Q0;
            Q0=makeQuery(id+"F34.imprint","IMPRINT",FACE,{"disambiguationData":[TD([[makeQuery(id+"F34.imprint","IMPRINT",EDGE,{"derivedFrom":sQuery(id+"F34.wireOp",EDGE,"E35")}),1.0]])]});
            extrude(context, id + "F35", {"entities" : qUnion([Q0]), "operationType" : NewBodyOperationType.ADD, "depth" : 10 * mm});
        }
        {
            var Q0;
            Q0=sQuery(id+"F2.wireOp",VERTEX,"E6");
            var Q1;
            Q1=makeQuery(id+"F1.opExtrude","SWEPT_BODY",BODY,{"disambiguationData":[OSD([sQuery(id+"F0.wireOp",EDGE,"E0.rect.bottom"),sQuery(id+"F0.wireOp",EDGE,"E0.rect.top"),sQuery(id+"F0.wireOp",EDGE,"E0.rect.left"),sQuery(id+"F0.wireOp",EDGE,"E0.rect.right")])]});
            hole(context, id + "F36", {"style" : HoleStyle.SIMPLE, "endStyle" : HoleEndStyle.BLIND, "holeDiameter" : 6 * mm, "holeDepth" : 18 * mm, "locations" : qUnion([Q0]), "scope" : qUnion([Q1])});
        }
        {
            var Q0;
            {var subQ0=sQuery(id+"F0.wireOp",EDGE,"E0.rect.top");Q0=makeQuery(id+"F7.imprint","IMPRINT",FACE,{"disambiguationData":[TD([[makeQuery(id+"F7.imprint","IMPRINT",EDGE,{"derivedFrom":makeQuery(id+"F1.opExtrude","CAP_EDGE",EDGE,{"disambiguationData":[OSD([subQ0])],"isStart":true})}),-1.0]])]});}
            var sketch = newSketch(context, id + "F37", { "sketchPlane" : qUnion([Q0])});
            skCircle(sketch, "E36.cCircle", {"center": v(-50, 16) * mm, "radius": 12 * mm, "construction": true});
            skLineSegment(sketch, "E36.0", {"start": v(-38, 22.93) * mm, "end": v(-38, 9.07) * mm});
            skLineSegment(sketch, "E36.1", {"start": v(-38, 9.07) * mm, "end": v(-50, 2.14) * mm});
            skLineSegment(sketch, "E36.2", {"start": v(-50, 2.14) * mm, "end": v(-62, 9.07) * mm});
            skLineSegment(sketch, "E36.3", {"start": v(-62, 9.07) * mm, "end": v(-62, 22.93) * mm});
            skLineSegment(sketch, "E36.4", {"start": v(-62, 22.93) * mm, "end": v(-50, 29.86) * mm});
            skLineSegment(sketch, "E36.5", {"start": v(-50, 29.86) * mm, "end": v(-38, 22.93) * mm});
            skPoint(sketch, "E36.0.midPoint", {"position": v(-38, 16) * mm});
            skCircle(sketch, "E37.cCircle", {"center": v(-18, 34) * mm, "radius": 12 * mm, "construction": true});
            skLineSegment(sketch, "E37.0", {"start": v(-5.15, 39.18) * mm, "end": v(-7.1, 25.46) * mm});
            skLineSegment(sketch, "E37.1", {"start": v(-7.1, 25.46) * mm, "end": v(-19.94, 20.28) * mm});
            skLineSegment(sketch, "E37.2", {"start": v(-19.94, 20.28) * mm, "end": v(-30.85, 28.82) * mm});
            skLineSegment(sketch, "E37.3", {"start": v(-30.85, 28.82) * mm, "end": v(-28.9, 42.54) * mm});
            skLineSegment(sketch, "E37.4", {"start": v(-28.9, 42.54) * mm, "end": v(-16.06, 47.72) * mm});
            skLineSegment(sketch, "E37.5", {"start": v(-16.06, 47.72) * mm, "end": v(-5.15, 39.18) * mm});
            skPoint(sketch, "E37.0.midPoint", {"position": v(-6.12, 32.32) * mm});
            skSolve(sketch);
        }
        {
            var Q0;
            Q0=qSketchRegion(id+"F37",true);
            extrude(context, id + "F38", {"entities" : qUnion([Q0]), "depth" : 12.6 * mm});
        }
        {
            var Q0;
            Q0=makeQuery(id+"F38.opExtrude","CAP_FACE",FACE,{"disambiguationData":[OSD([sQuery(id+"F37.wireOp",EDGE,"E36.0"),sQuery(id+"F37.wireOp",EDGE,"E36.1"),sQuery(id+"F37.wireOp",EDGE,"E36.2"),sQuery(id+"F37.wireOp",EDGE,"E36.3"),sQuery(id+"F37.wireOp",EDGE,"E36.4"),sQuery(id+"F37.wireOp",EDGE,"E36.5")])],"isStart":false});
            var sketch = newSketch(context, id + "F39", { "sketchPlane" : qUnion([Q0])});
            skCircle(sketch, "E38", {"center": v(-50, 16) * mm, "radius": 4 * mm});
            skPoint(sketch, "E38.centerSnap0", {"position": v(-62, 16) * mm});
            skSolve(sketch);
        }
        {
            var Q0;
            Q0=makeQuery(id+"F39.imprint","IMPRINT",FACE,{"disambiguationData":[TD([[makeQuery(id+"F39.imprint","IMPRINT",EDGE,{"derivedFrom":sQuery(id+"F39.wireOp",EDGE,"E38")}),1.0]])]});
            extrude(context, id + "F40", {"entities" : qUnion([Q0]), "operationType" : NewBodyOperationType.ADD, "depth" : 39 * mm});
        }
        {
            var Q0;
            Q0=makeQuery(id+"F40.opExtrude","CAP_FACE",FACE,{"disambiguationData":[OSD([sQuery(id+"F39.wireOp",EDGE,"E38")])],"isStart":false});
            var sketch = newSketch(context, id + "F41", { "sketchPlane" : qUnion([Q0])});
            skCircle(sketch, "E39.cCircle", {"center": v(-50, 16) * mm, "radius": 8.5 * mm, "construction": true});
            skLineSegment(sketch, "E39.0", {"start": v(-45.41, 24.68) * mm, "end": v(-40.2, 16.37) * mm});
            skLineSegment(sketch, "E39.1", {"start": v(-40.2, 16.37) * mm, "end": v(-44.78, 7.69) * mm});
            skLineSegment(sketch, "E39.2", {"start": v(-44.78, 7.69) * mm, "end": v(-54.59, 7.32) * mm});
            skLineSegment(sketch, "E39.3", {"start": v(-54.59, 7.32) * mm, "end": v(-59.8, 15.63) * mm});
            skLineSegment(sketch, "E39.4", {"start": v(-59.8, 15.63) * mm, "end": v(-55.22, 24.31) * mm});
            skLineSegment(sketch, "E39.5", {"start": v(-55.22, 24.31) * mm, "end": v(-45.41, 24.68) * mm});
            skPoint(sketch, "E39.0.midPoint", {"position": v(-42.8, 20.52) * mm});
            skSolve(sketch);
        }
        {
            var Q0;
            Q0=makeQuery(id+"F41.imprint","IMPRINT",FACE,{"disambiguationData":[TD([[makeQuery(id+"F41.imprint","IMPRINT",EDGE,{"derivedFrom":sQuery(id+"F41.wireOp",EDGE,"E39.0")}),-1.0]])]});
            var Q1;
            Q1=makeQuery(id+"F41.imprint","IMPRINT",FACE,{"disambiguationData":[TD([[makeQuery(id+"F41.imprint","IMPRINT",EDGE,{"derivedFrom":makeQuery(id+"F40.opExtrude","CAP_EDGE",EDGE,{"disambiguationData":[OSD([sQuery(id+"F39.wireOp",EDGE,"E38")])],"isStart":false})}),1.0]])]});
            extrude(context, id + "F42", {"entities" : qUnion([Q0, Q1]), "operationType" : NewBodyOperationType.ADD, "depth" : 6.3 * mm});
        }
        {
            var Q0;
            Q0=makeQuery(id+"F38.opExtrude","CAP_FACE",FACE,{"disambiguationData":[OSD([sQuery(id+"F37.wireOp",EDGE,"E37.0"),sQuery(id+"F37.wireOp",EDGE,"E37.1"),sQuery(id+"F37.wireOp",EDGE,"E37.2"),sQuery(id+"F37.wireOp",EDGE,"E37.3"),sQuery(id+"F37.wireOp",EDGE,"E37.4"),sQuery(id+"F37.wireOp",EDGE,"E37.5")])],"isStart":false});
            var sketch = newSketch(context, id + "F43", { "sketchPlane" : qUnion([Q0])});
            skLineSegment(sketch, "E40", {"start": v(-13.52, 22.87) * mm, "end": v(-22.48, 45.13) * mm, "construction": true});
            skCircle(sketch, "E41", {"center": v(-18, 34) * mm, "radius": 4 * mm});
            skSolve(sketch);
        }
        {
            var Q0;
            Q0=makeQuery(id+"F43.imprint","IMPRINT",FACE,{"disambiguationData":[TD([[makeQuery(id+"F43.imprint","IMPRINT",EDGE,{"derivedFrom":sQuery(id+"F43.wireOp",EDGE,"E41")}),1.0]])]});
            extrude(context, id + "F44", {"entities" : qUnion([Q0]), "operationType" : NewBodyOperationType.ADD, "depth" : 39 * mm});
        }
        {
            var Q0;
            Q0=makeQuery(id+"F44.opExtrude","CAP_FACE",FACE,{"disambiguationData":[OSD([sQuery(id+"F43.wireOp",EDGE,"E41")])],"isStart":false});
            var sketch = newSketch(context, id + "F45", { "sketchPlane" : qUnion([Q0])});
            skCircle(sketch, "E42.cCircle", {"center": v(-18, 34) * mm, "radius": 8.5 * mm, "construction": true});
            skLineSegment(sketch, "E42.0", {"start": v(-9.5, 38.9) * mm, "end": v(-9.5, 29.1) * mm});
            skLineSegment(sketch, "E42.1", {"start": v(-9.5, 29.1) * mm, "end": v(-18, 24.19) * mm});
            skLineSegment(sketch, "E42.2", {"start": v(-18, 24.19) * mm, "end": v(-26.5, 29.1) * mm});
            skLineSegment(sketch, "E42.3", {"start": v(-26.5, 29.1) * mm, "end": v(-26.5, 38.9) * mm});
            skLineSegment(sketch, "E42.4", {"start": v(-26.5, 38.9) * mm, "end": v(-18, 43.81) * mm});
            skLineSegment(sketch, "E42.5", {"start": v(-18, 43.81) * mm, "end": v(-9.5, 38.9) * mm});
            skPoint(sketch, "E42.0.midPoint", {"position": v(-9.5, 34) * mm});
            skSolve(sketch);
        }
        {
            var Q0;
            Q0=makeQuery(id+"F45.imprint","IMPRINT",FACE,{"disambiguationData":[TD([[makeQuery(id+"F45.imprint","IMPRINT",EDGE,{"derivedFrom":sQuery(id+"F45.wireOp",EDGE,"E42.0")}),-1.0]])]});
            var Q1;
            Q1=makeQuery(id+"F45.imprint","IMPRINT",FACE,{"disambiguationData":[TD([[makeQuery(id+"F45.imprint","IMPRINT",EDGE,{"derivedFrom":makeQuery(id+"F44.opExtrude","CAP_EDGE",EDGE,{"disambiguationData":[OSD([sQuery(id+"F43.wireOp",EDGE,"E41")])],"isStart":false})}),1.0]])]});
            extrude(context, id + "F46", {"entities" : qUnion([Q0, Q1]), "operationType" : NewBodyOperationType.ADD, "depth" : 6.3 * mm});
        }
        {
            var Q0;
            Q0=sQuery(id+"F2.wireOp",VERTEX,"E2.center");
            var Q1;
            Q1=sQuery(id+"F2.wireOp",VERTEX,"E1.center");
            var Q2;
            Q2=makeQuery(id+"F1.opExtrude","SWEPT_BODY",BODY,{"disambiguationData":[OSD([sQuery(id+"F0.wireOp",EDGE,"E0.rect.bottom"),sQuery(id+"F0.wireOp",EDGE,"E0.rect.top"),sQuery(id+"F0.wireOp",EDGE,"E0.rect.left"),sQuery(id+"F0.wireOp",EDGE,"E0.rect.right")])]});
            hole(context, id + "F47", {"style" : HoleStyle.SIMPLE, "endStyle" : HoleEndStyle.BLIND, "holeDiameter" : 5 * mm, "holeDepth" : 6 * mm, "locations" : qUnion([Q0, Q1]), "scope" : qUnion([Q2])});
        }
    });
